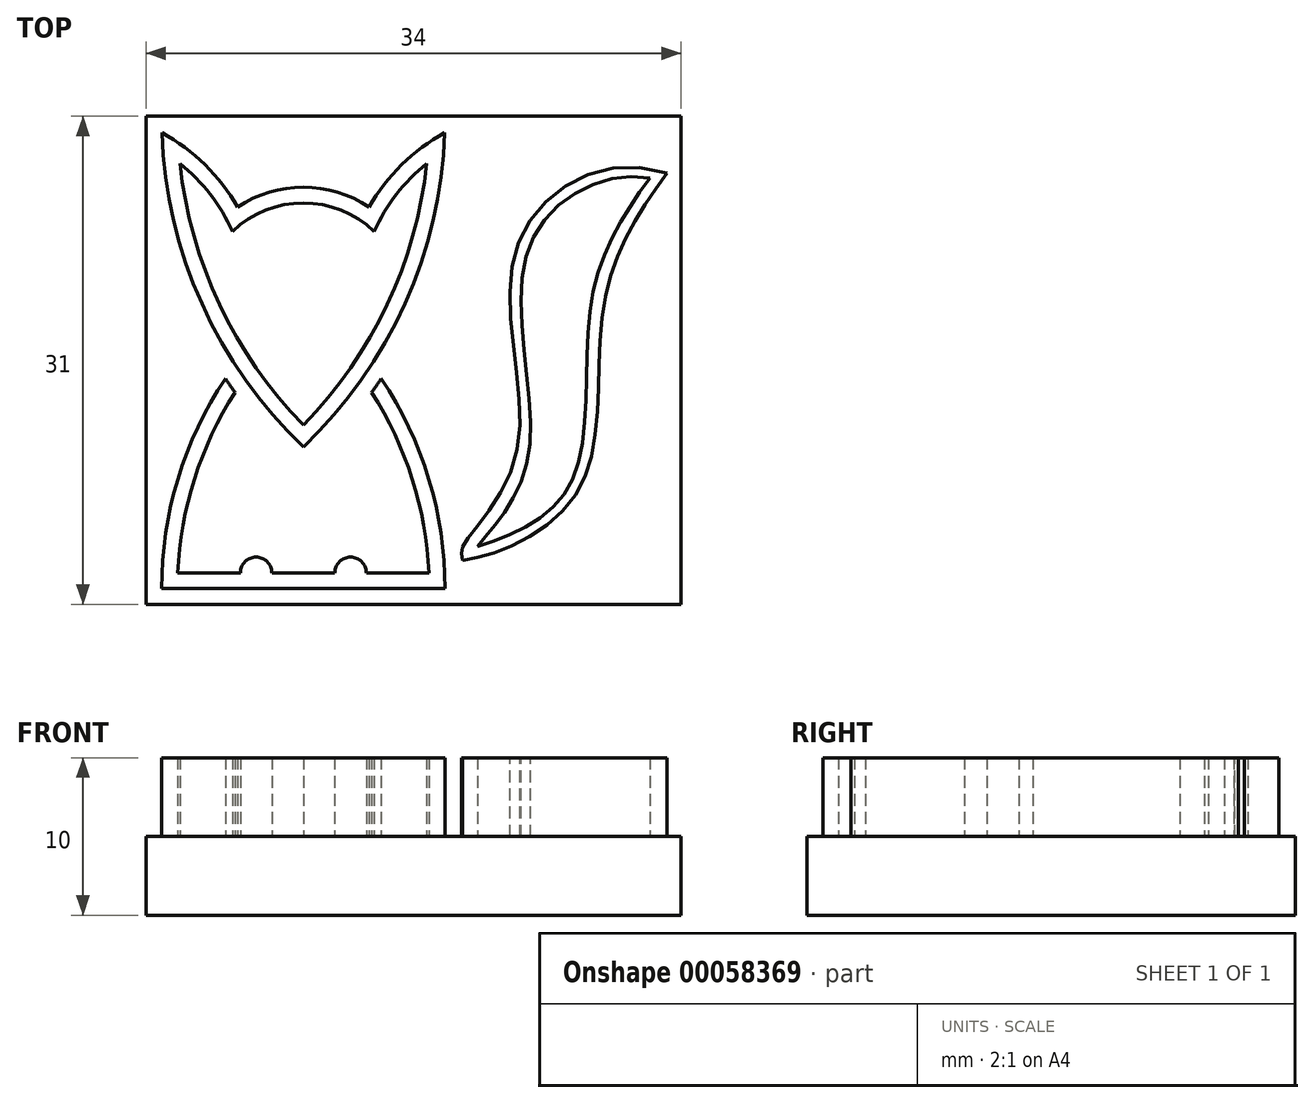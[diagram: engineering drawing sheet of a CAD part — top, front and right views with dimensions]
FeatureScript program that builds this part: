
annotation { "Feature Type Name" : "Feature", "Feature Type Description" : "" }
export const myFeature = defineFeature(function(context is Context, id is Id, definition is map)
    precondition{}
    {
        {
            var Q0;
            Q0=qCreatedBy(makeId("Top.planeOp"),FACE);
            var sketch = newSketch(context, id + "F0", { "sketchPlane" : qUnion([Q0])});
            skLineSegment(sketch, "E0.rect.bottom", {"start": v(20, 18.56) * mm, "end": v(-20, 18.56) * mm});
            skLineSegment(sketch, "E0.rect.top", {"start": v(20, -21.44) * mm, "end": v(-20, -21.44) * mm});
            skLineSegment(sketch, "E0.rect.left", {"start": v(20, 18.56) * mm, "end": v(20, -21.44) * mm});
            skLineSegment(sketch, "E0.rect.right", {"start": v(-20, 18.56) * mm, "end": v(-20, -21.44) * mm});
            skPoint(sketch, "E0.rect.middle", {"position": v(0, -1.44) * mm});
            skSolve(sketch);
        }
        {
            var Q0;
            Q0=makeQuery(id+"F0.imprint","IMPRINT",FACE,{"disambiguationData":[TD([[makeQuery(id+"F0.imprint","IMPRINT",EDGE,{"derivedFrom":sQuery(id+"F0.wireOp",EDGE,"E0.rect.bottom")}),1.0]])]});
            extrude(context, id + "F1", {"entities" : qUnion([Q0]), "depth" : 5 * mm});
        }
        {
            var Q0;
            Q0=makeQuery(id+"F1.opExtrude","CAP_FACE",FACE,{"disambiguationData":[OSD([sQuery(id+"F0.wireOp",EDGE,"E0.rect.bottom"),sQuery(id+"F0.wireOp",EDGE,"E0.rect.top"),sQuery(id+"F0.wireOp",EDGE,"E0.rect.left"),sQuery(id+"F0.wireOp",EDGE,"E0.rect.right")])],"isStart":false});
            var sketch = newSketch(context, id + "F2", { "sketchPlane" : qUnion([Q0])});
            skArc(sketch, "E1", {"start": v(-9.29, 38.86) * mm, "mid": v(-9.64, 39.2) * mm, "end": v(-10, 39.56) * mm});
            skLineSegment(sketch, "E2", {"start": v(0, 0) * mm, "end": v(0, -1.54) * mm});
            skArc(sketch, "E3", {"start": v(-18.98, 17.51) * mm, "mid": v(-16.45, 6.66) * mm, "end": v(-10, -2.44) * mm});
            skArc(sketch, "E4", {"start": v(-14.17, 12.8) * mm, "mid": v(-16.25, 15.48) * mm, "end": v(-18.98, 17.51) * mm});
            skArc(sketch, "E5", {"start": v(-6.3, 1.21) * mm, "mid": v(-6.08, 0.76) * mm, "end": v(-5.83, 0.32) * mm});
            skArc(sketch, "E6", {"start": v(-14.58, 0.62) * mm, "mid": v(-14.38, 0.47) * mm, "end": v(-14.17, 0.32) * mm});
            skArc(sketch, "E7", {"start": v(-14.5, 11.25) * mm, "mid": v(-15.91, 13.6) * mm, "end": v(-17.84, 15.56) * mm});
            skArc(sketch, "E8", {"start": v(-5.5, 1.87) * mm, "mid": v(-5.28, 1.4) * mm, "end": v(-5.03, 0.94) * mm});
            skArc(sketch, "E9", {"start": v(-14.78, 2.15) * mm, "mid": v(-14.27, 1.65) * mm, "end": v(-13.7, 1.21) * mm});
            skArc(sketch, "E10.trimOffspring", {"start": v(-5.83, 12.8) * mm, "mid": v(-10, 14.06) * mm, "end": v(-14.17, 12.8) * mm});
            skArc(sketch, "E11.trimOffspring", {"start": v(-5.5, 11.25) * mm, "mid": v(-10, 13.06) * mm, "end": v(-14.5, 11.25) * mm});
            skArc(sketch, "E12", {"start": v(-10, 38.15) * mm, "mid": v(-10.35, 38.5) * mm, "end": v(-10.71, 38.86) * mm});
            skArc(sketch, "E13", {"start": v(-17.84, 15.56) * mm, "mid": v(-15.32, 6.6) * mm, "end": v(-10, -1.04) * mm});
            skArc(sketch, "E14.trimOffspring", {"start": v(-14.97, 0.94) * mm, "mid": v(-14.72, 1.4) * mm, "end": v(-14.5, 1.87) * mm});
            skArc(sketch, "E15.trimOffspring", {"start": v(-2.16, 15.56) * mm, "mid": v(-4.09, 13.6) * mm, "end": v(-5.5, 11.25) * mm});
            skArc(sketch, "E16.trimOffspring", {"start": v(-6.3, 1.21) * mm, "mid": v(-5.73, 1.65) * mm, "end": v(-5.22, 2.15) * mm});
            skArc(sketch, "E17.trimOffspring", {"start": v(-5.83, 0.32) * mm, "mid": v(-5.62, 0.47) * mm, "end": v(-5.42, 0.62) * mm});
            skArc(sketch, "E18.trimOffspring", {"start": v(-10.1, -0.94) * mm, "mid": v(-10, -0.94) * mm, "end": v(-9.9, -0.94) * mm});
            skArc(sketch, "E19.trimOffspring", {"start": v(-10, -1.04) * mm, "mid": v(-4.68, 6.6) * mm, "end": v(-2.16, 15.56) * mm});
            skArc(sketch, "E20.trimOffspring", {"start": v(-9.29, 38.86) * mm, "mid": v(-9.65, 38.5) * mm, "end": v(-10, 38.15) * mm});
            skArc(sketch, "E21.trimOffspring", {"start": v(-14.17, 0.32) * mm, "mid": v(-13.92, 0.76) * mm, "end": v(-13.7, 1.21) * mm});
            skArc(sketch, "E22.trimOffspring", {"start": v(-1.02, 17.51) * mm, "mid": v(-3.75, 15.48) * mm, "end": v(-5.83, 12.8) * mm});
            skArc(sketch, "E23.trimOffspring", {"start": v(-10, 39.56) * mm, "mid": v(-10.36, 39.2) * mm, "end": v(-10.71, 38.86) * mm});
            skArc(sketch, "E24.trimOffspring", {"start": v(-10, -2.44) * mm, "mid": v(-3.55, 6.66) * mm, "end": v(-1.02, 17.51) * mm});
            skArc(sketch, "E25", {"start": v(-14.33, 2.78) * mm, "mid": v(-17.8, -3.96) * mm, "end": v(-19, -11.44) * mm});
            skArc(sketch, "E26", {"start": v(-1, -11.44) * mm, "mid": v(-2.2, -3.96) * mm, "end": v(-5.67, 2.78) * mm});
            skArc(sketch, "E27", {"start": v(-10, -28.88) * mm, "mid": v(-4.1, -21.03) * mm, "end": v(-2, -11.44) * mm});
            skArc(sketch, "E28", {"start": v(-13.74, 1.9) * mm, "mid": v(-16.75, -3.97) * mm, "end": v(-17.98, -10.44) * mm});
            skLineSegment(sketch, "E29", {"start": v(-19, -11.44) * mm, "end": v(-1, -11.44) * mm});
            skLineSegment(sketch, "E30", {"start": v(-17.98, -10.44) * mm, "end": v(-14, -10.44) * mm});
            skArc(sketch, "E31.trimOffspring", {"start": v(-18, -11.44) * mm, "mid": v(-15.9, -21.03) * mm, "end": v(-10, -28.88) * mm});
            skPoint(sketch, "E32.orphan", {"position": v(-25, -10.44) * mm});
            skArc(sketch, "E33.trimOffspring", {"start": v(-2.02, -10.44) * mm, "mid": v(-3.25, -3.97) * mm, "end": v(-6.26, 1.9) * mm});
            skArc(sketch, "E34", {"start": v(-12, -10.44) * mm, "mid": v(-13, -9.44) * mm, "end": v(-14, -10.44) * mm});
            skArc(sketch, "E35", {"start": v(-6, -10.44) * mm, "mid": v(-7, -9.44) * mm, "end": v(-8, -10.44) * mm});
            skLineSegment(sketch, "E36.trimOffspring", {"start": v(-12, -10.44) * mm, "end": v(-8, -10.44) * mm});
            skLineSegment(sketch, "E37.trimOffspring", {"start": v(-6, -10.44) * mm, "end": v(-2.02, -10.44) * mm});
            skArc(sketch, "E38", {"start": v(-1.1, -9.32) * mm, "mid": v(21.62, 46.22) * mm, "end": v(-2.14, -8.87) * mm});
            skArc(sketch, "E39", {"start": v(-17.86, -8.87) * mm, "mid": v(-41.62, 46.22) * mm, "end": v(-18.9, -9.32) * mm});
            skSolve(sketch);
        }
        {
            var Q0;
            {var subQ7=sQuery(id+"F2.wireOp",EDGE,"E4");Q0=makeQuery(id+"F2.imprint","IMPRINT",FACE,{"disambiguationData":[TD([[makeQuery(id+"F2.imprint","IMPRINT",EDGE,{"derivedFrom":subQ7}),1.0]])]});}
            var Q1;
            {var subQ8=sQuery(id+"F2.wireOp",EDGE,"E30");Q1=makeQuery(id+"F2.imprint","IMPRINT",FACE,{"disambiguationData":[TD([[makeQuery(id+"F2.imprint","IMPRINT",EDGE,{"derivedFrom":subQ8}),-1.0]])]});}
            extrude(context, id + "F3", {"entities" : qUnion([Q0, Q1]), "operationType" : NewBodyOperationType.ADD, "depth" : 5 * mm});
        }
        {
            var Q0;
            {var subQ3=sQuery(id+"F2.wireOp",EDGE,"E26");var subQ5=sQuery(id+"F2.wireOp",EDGE,"E24.trimOffspring");var subQ6=makeQuery(id+"F2.imprint","INTERSECT",VERTEX,{"derivedFrom":[subQ5,subQ3]});Q0=makeQuery(id+"F2.imprint","IMPRINT",FACE,{"disambiguationData":[TD([[makeQuery(id+"F2.imprint","IMPRINT",EDGE,{"disambiguationData":[TD([[subQ6,-1.0]])],"derivedFrom":subQ5}),-1.0]])]});}
            var sketch = newSketch(context, id + "F4", { "sketchPlane" : qUnion([Q0])});
            skFitSpline(sketch, "E40", {"points": [v(0.12, -9.64) * mm, v(0.13, -8.78) * mm, v(3.52, -2.92) * mm, v(3.56, 10.25) * mm, v(13.09, 14.94) * mm], "startDerivative": vector(-1.44, 13.02) * mm, "endDerivative": vector(40.31, -13.35) * mm});
            skFitSpline(sketch, "E41", {"points": [v(0.12, -9.64) * mm, v(7.32, -5.45) * mm, v(9.06, 6.48) * mm, v(13.09, 14.94) * mm], "startDerivative": vector(19.08, 2.26) * mm, "endDerivative": vector(16.36, 22.03) * mm});
            skFitSpline(sketch, "E42", {"points": [v(1.06, -8.75) * mm, v(7.02, -4.66) * mm, v(8.3, 6.8) * mm, v(12, 14.65) * mm], "startDerivative": vector(24.2, 7.3) * mm, "endDerivative": vector(14.97, 21) * mm});
            skFitSpline(sketch, "E43", {"points": [v(12, 14.65) * mm, v(4.4, 10.42) * mm, v(4.3, -2.97) * mm, v(1.06, -8.75) * mm], "startDerivative": vector(-26.46, 4.73) * mm, "endDerivative": vector(-11, -13.43) * mm});
            skSolve(sketch);
        }
        {
            var Q0;
            Q0 = qSketchRegion(id + "F4", true);
            extrude(context, id + "F5", {"entities" : qUnion([Q0]), "operationType" : NewBodyOperationType.ADD, "depth" : 5 * mm});
        }
        {
            var Q0;
            {var subQ11=sQuery(id+"F0.wireOp",EDGE,"E0.rect.right");var subQ14=sQuery(id+"F0.wireOp",EDGE,"E0.rect.left");var subQ17=sQuery(id+"F0.wireOp",EDGE,"E0.rect.top");var subQ21=sQuery(id+"F0.wireOp",EDGE,"E0.rect.bottom");var subQ22=makeQuery(id+"F1.opExtrude","SWEPT_FACE",FACE,{"disambiguationData":[OSD([subQ21])]});Q0=makeQuery(id+"F5.boolean.opBoolean","SPLIT",FACE,{"disambiguationData":[TD([subQ22])],"derivedFrom":makeQuery(id+"F3.boolean.opBoolean","SPLIT",FACE,{"disambiguationData":[TD([subQ22])],"derivedFrom":makeQuery(id+"F1.opExtrude","CAP_FACE",FACE,{"disambiguationData":[OSD([subQ21,subQ17,subQ14,subQ11])],"isStart":false})})});}
            var sketch = newSketch(context, id + "F6", { "sketchPlane" : qUnion([Q0])});
            skLineSegment(sketch, "E44.bottom", {"start": v(20, -21.44) * mm, "end": v(-20, -21.44) * mm});
            skLineSegment(sketch, "E44.top", {"start": v(20, 18.56) * mm, "end": v(-20, 18.56) * mm});
            skLineSegment(sketch, "E44.left", {"start": v(20, -21.44) * mm, "end": v(20, 18.56) * mm});
            skLineSegment(sketch, "E44.right", {"start": v(-20, -21.44) * mm, "end": v(-20, 18.56) * mm});
            skLineSegment(sketch, "E45.bottom", {"start": v(-20, 18.56) * mm, "end": v(14, 18.56) * mm});
            skLineSegment(sketch, "E45.top", {"start": v(-20, -12.44) * mm, "end": v(14, -12.44) * mm});
            skLineSegment(sketch, "E45.left", {"start": v(-20, 18.56) * mm, "end": v(-20, -12.44) * mm});
            skLineSegment(sketch, "E45.right", {"start": v(14, 18.56) * mm, "end": v(14, -12.44) * mm});
            skSolve(sketch);
        }
        {
            var Q0;
            Q0=makeQuery(id+"F6.imprint","IMPRINT",FACE,{"disambiguationData":[TD([[makeQuery(id+"F6.imprint","IMPRINT",EDGE,{"derivedFrom":sQuery(id+"F6.wireOp",EDGE,"E44.bottom")}),-1.0]])]});
            extrude(context, id + "F7", {"entities" : qUnion([Q0]), "operationType" : NewBodyOperationType.REMOVE, "endBound" : BoundingType.UP_TO_NEXT, "oppositeDirection" : true, "depth" : 25 * mm});
        }
    });
